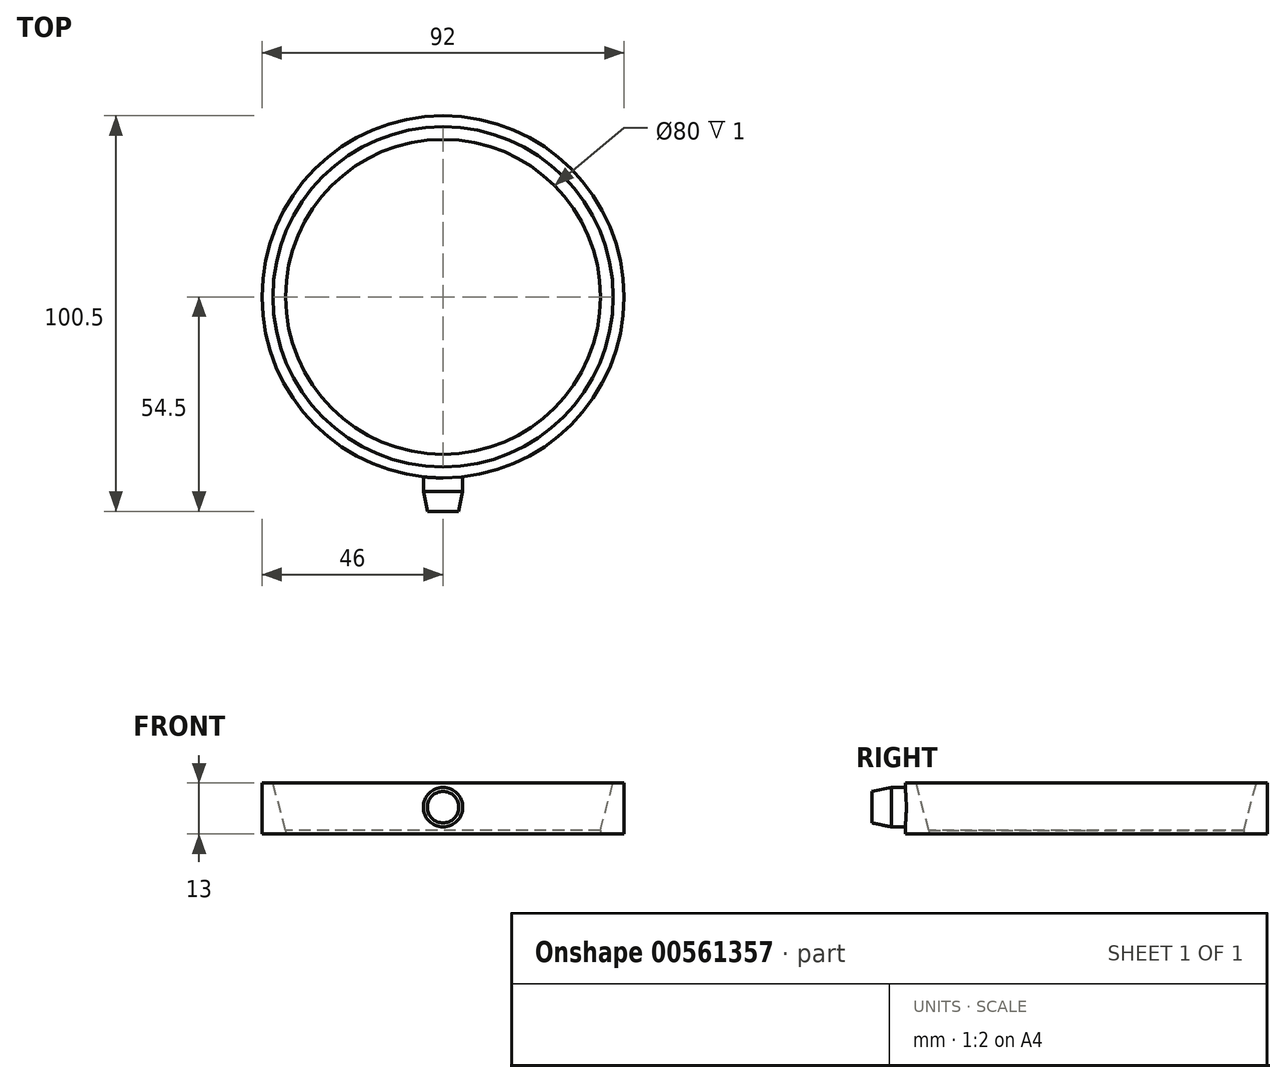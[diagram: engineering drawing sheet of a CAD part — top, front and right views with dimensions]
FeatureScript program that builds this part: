
annotation { "Feature Type Name" : "Feature", "Feature Type Description" : "" }
export const myFeature = defineFeature(function(context is Context, id is Id, definition is map)
    precondition{}
    {
        {
            var Q0;
            Q0=qCreatedBy(makeId("Top.planeOp"),FACE);
            var sketch = newSketch(context, id + "F0", { "sketchPlane" : qUnion([Q0])});
            skCircle(sketch, "E0", {"center": v(0, 0) * mm, "radius": 40 * mm});
            skCircle(sketch, "E1.0", {"center": v(0, 0) * mm, "radius": 46 * mm});
            skSolve(sketch);
        }
        {
            var Q0;
            Q0=makeQuery(id+"F0.imprint","IMPRINT",FACE,{"disambiguationData":[TD([[makeQuery(id+"F0.imprint","IMPRINT",EDGE,{"derivedFrom":sQuery(id+"F0.wireOp",EDGE,"E0")}),-1.0]])]});
            extrude(context, id + "F1", {"entities" : qUnion([Q0]), "depth" : 13 * mm, "offsetDistance" : 25 * mm});
        }
        {
            var Q0;
            Q0=qCreatedBy(makeId("Front.planeOp"),FACE);
            cPlane(context, id + "F2", {"entities" : qUnion([Q0]), "cplaneType" : CPlaneType.OFFSET, "offset" : 44.5 * mm, "width" : 150 * mm, "height" : 150 * mm});
        }
        {
            var Q0;
            Q0=qCreatedBy(id+"F2.planeOp",FACE);
            var sketch = newSketch(context, id + "F3", { "sketchPlane" : qUnion([Q0])});
            skCircle(sketch, "E2", {"center": v(0, 6.84) * mm, "radius": 5 * mm});
            skSolve(sketch);
        }
        {
            var Q0;
            Q0 = qSketchRegion(id + "F3", true);
            extrude(context, id + "F4", {"entities" : qUnion([Q0]), "operationType" : NewBodyOperationType.ADD, "depth" : 10 * mm, "offsetDistance" : 25 * mm});
        }
        {
            var Q0;
            Q0=makeQuery(id+"F1.opExtrude","CAP_EDGE",EDGE,{"disambiguationData":[OSD([sQuery(id+"F0.wireOp",EDGE,"E0")])],"isStart":false});
            chamfer(context, id + "F5", {"entities" : qUnion([Q0]), "chamferType" : ChamferType.OFFSET_ANGLE, "width" : 12 * mm, "oppositeDirection" : false, "angle" : 15 * degree, "tangentPropagation" : true});
        }
        {
            var Q0;
            Q0=makeQuery(id+"F4.opExtrude","CAP_EDGE",EDGE,{"disambiguationData":[OSD([sQuery(id+"F3.wireOp",EDGE,"E2")])],"isStart":false});
            chamfer(context, id + "F6", {"entities" : qUnion([Q0]), "chamferType" : ChamferType.TWO_OFFSETS, "width1" : 1 * mm, "oppositeDirection" : false, "width2" : 5 * mm, "tangentPropagation" : true});
        }
    });
